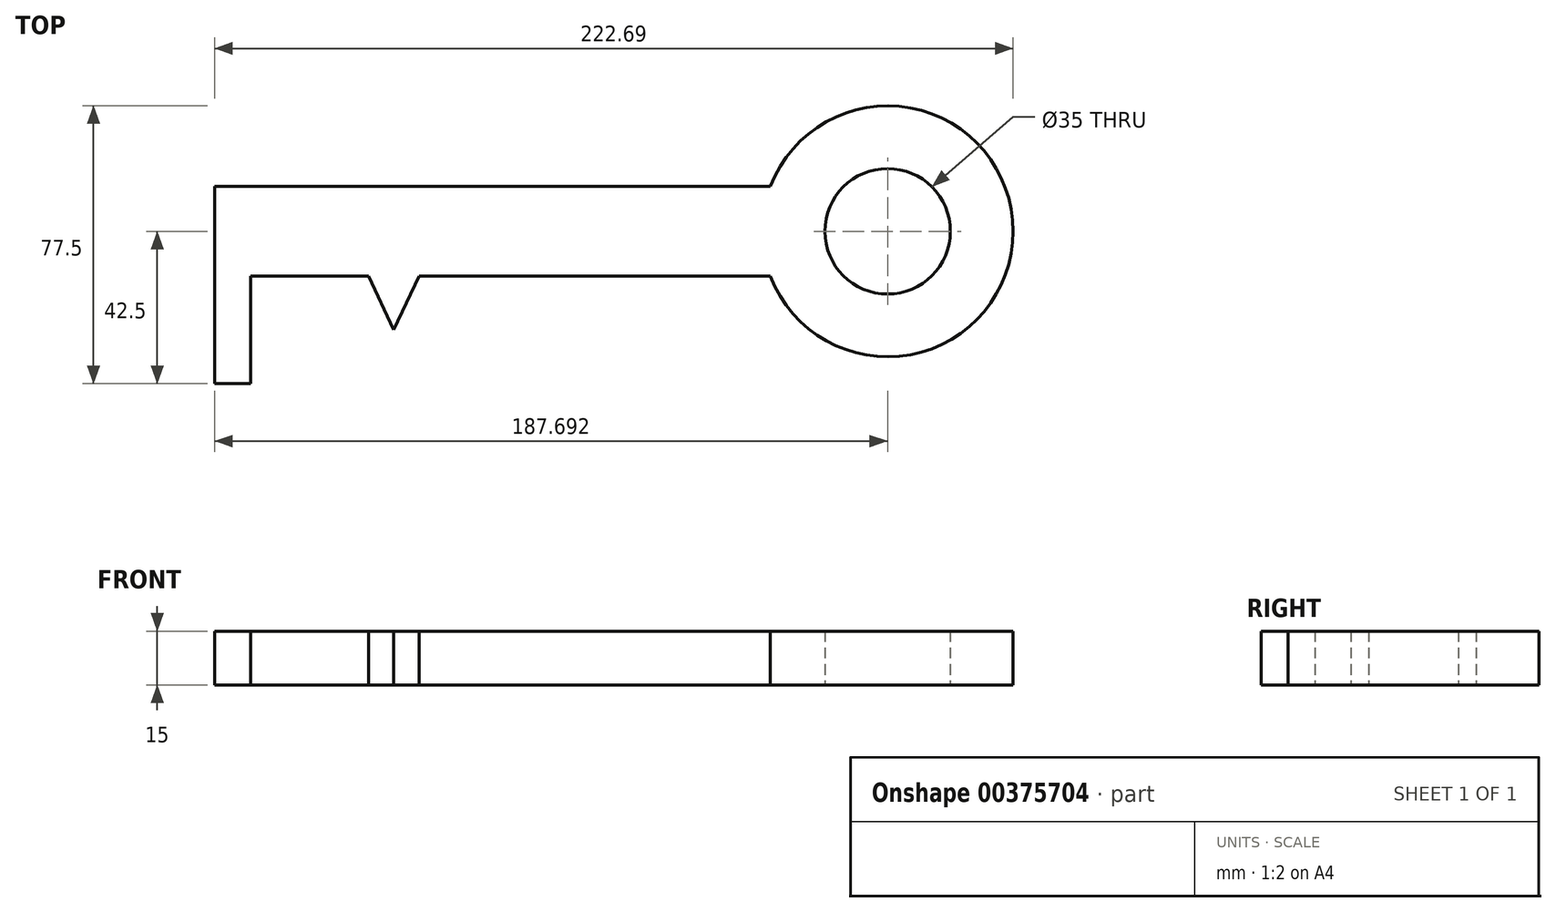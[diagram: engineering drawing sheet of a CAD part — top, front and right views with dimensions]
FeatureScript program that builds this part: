
annotation { "Feature Type Name" : "Feature", "Feature Type Description" : "" }
export const myFeature = defineFeature(function(context is Context, id is Id, definition is map)
    precondition{}
    {
        {
            var Q0;
            Q0=qCreatedBy(makeId("Top.planeOp"),FACE);
            var sketch = newSketch(context, id + "F0", { "sketchPlane" : qUnion([Q0])});
            skLineSegment(sketch, "E0.bottom", {"start": v(0, 0) * mm, "end": v(-155, 0) * mm});
            skLineSegment(sketch, "E0.top", {"start": v(0, 25) * mm, "end": v(-155, 25) * mm});
            skLineSegment(sketch, "E0.left", {"start": v(0, 0) * mm, "end": v(0, 25) * mm});
            skLineSegment(sketch, "E0.right", {"start": v(-155, 0) * mm, "end": v(-155, 25) * mm});
            skLineSegment(sketch, "E1.bottom", {"start": v(-155, -30) * mm, "end": v(-145, -30) * mm});
            skLineSegment(sketch, "E1.top", {"start": v(-155, 0) * mm, "end": v(-145, 0) * mm});
            skLineSegment(sketch, "E1.left", {"start": v(-155, -30) * mm, "end": v(-155, 0) * mm});
            skLineSegment(sketch, "E1.right", {"start": v(-145, -30) * mm, "end": v(-145, 0) * mm});
            skLineSegment(sketch, "E2.bottom", {"start": v(-130, 0) * mm, "end": v(-122, 0) * mm});
            skLineSegment(sketch, "E2.top", {"start": v(-130, -15) * mm, "end": v(-122, -15) * mm});
            skLineSegment(sketch, "E2.left", {"start": v(-130, 0) * mm, "end": v(-130, -15) * mm});
            skLineSegment(sketch, "E2.right", {"start": v(-122, 0) * mm, "end": v(-122, -15) * mm});
            skLineSegment(sketch, "E3", {"start": v(-112, 0) * mm, "end": v(-105, -15) * mm});
            skLineSegment(sketch, "E4", {"start": v(-105, -15) * mm, "end": v(-98, 0) * mm});
            skArc(sketch, "E5", {"start": v(0, 0) * mm, "mid": v(67.7, 12.5) * mm, "end": v(0, 25) * mm});
            skCircle(sketch, "E6", {"center": v(32.7, 12.5) * mm, "radius": 17.5 * mm});
            skLineSegment(sketch, "E7", {"start": v(32.7, 12.5) * mm, "end": v(-155, 12.5) * mm, "construction": true});
            skSolve(sketch);
        }
        {
            var Q0;
            Q0=makeQuery(id+"F0.imprint","IMPRINT",FACE,{"disambiguationData":[TD([[makeQuery(id+"F0.imprint","IMPRINT",EDGE,{"derivedFrom":sQuery(id+"F0.wireOp",EDGE,"E1.bottom")}),1.0]])]});
            var Q1;
            Q1=makeQuery(id+"F0.imprint","IMPRINT",FACE,{"disambiguationData":[TD([[makeQuery(id+"F0.imprint","IMPRINT",EDGE,{"derivedFrom":sQuery(id+"F0.wireOp",EDGE,"E2.bottom")}),-1.0]])]});
            var Q2;
            Q2=makeQuery(id+"F0.imprint","IMPRINT",FACE,{"disambiguationData":[TD([[makeQuery(id+"F0.imprint","IMPRINT",EDGE,{"derivedFrom":sQuery(id+"F0.wireOp",EDGE,"E0.left")}),-1.0]])]});
            var Q3;
            Q3=makeQuery(id+"F0.imprint","IMPRINT",FACE,{"disambiguationData":[TD([[makeQuery(id+"F0.imprint","IMPRINT",EDGE,{"derivedFrom":sQuery(id+"F0.wireOp",EDGE,"E0.top")}),1.0]])]});
            var Q4;
            {var subQ0=sQuery(id+"F0.wireOp",EDGE,"E3");Q4=makeQuery(id+"F0.imprint","IMPRINT",FACE,{"disambiguationData":[TD([[makeQuery(id+"F0.imprint","IMPRINT",EDGE,{"derivedFrom":subQ0}),1.0]])]});}
            extrude(context, id + "F1", {"entities" : qUnion([Q0, Q1, Q2, Q3, Q4]), "depth" : 15 * mm});
        }
    });
